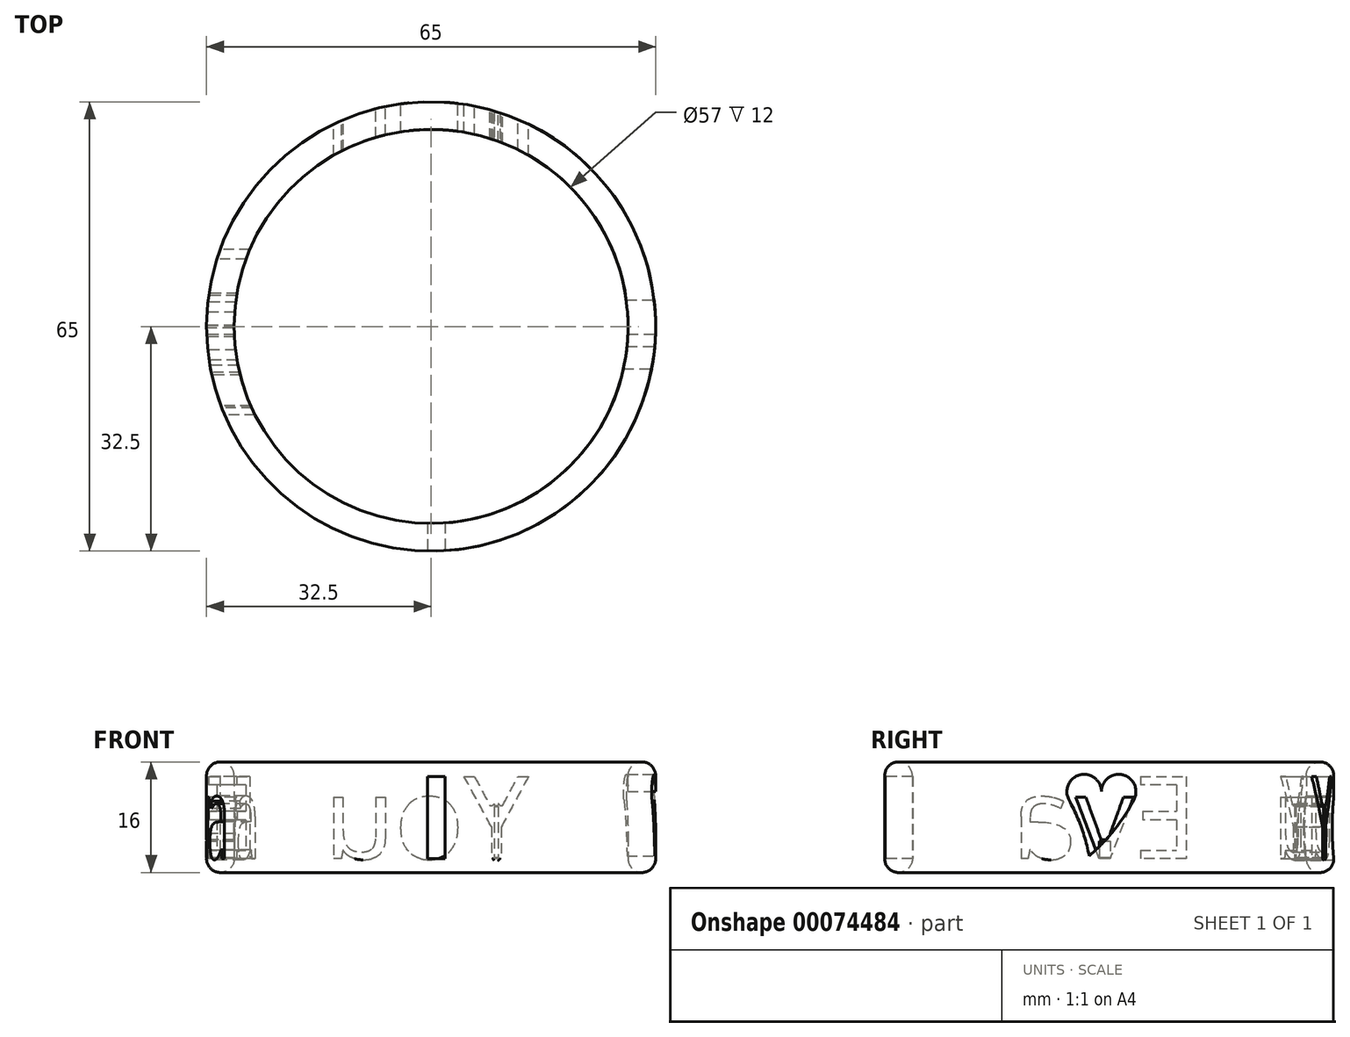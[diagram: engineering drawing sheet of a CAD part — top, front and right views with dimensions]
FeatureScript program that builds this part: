
annotation { "Feature Type Name" : "Feature", "Feature Type Description" : "" }
export const myFeature = defineFeature(function(context is Context, id is Id, definition is map)
    precondition{}
    {
        {
            var Q0;
            Q0=qCreatedBy(makeId("Top.planeOp"),FACE);
            var sketch = newSketch(context, id + "F0", { "sketchPlane" : qUnion([Q0])});
            skCircle(sketch, "E0", {"center": v(0, 0) * mm, "radius": 28.5 * mm});
            skCircle(sketch, "E1", {"center": v(0, 0) * mm, "radius": 32.5 * mm});
            skSolve(sketch);
        }
        {
            var Q0;
            Q0=makeQuery(id+"F0.imprint","IMPRINT",FACE,{"disambiguationData":[TD([[makeQuery(id+"F0.imprint","IMPRINT",EDGE,{"derivedFrom":sQuery(id+"F0.wireOp",EDGE,"E0")}),-1.0]])]});
            extrude(context, id + "F1", {"entities" : qUnion([Q0]), "depth" : 16 * mm});
        }
        {
            var Q0;
            Q0=qCreatedBy(makeId("Front.planeOp"),FACE);
            cPlane(context, id + "F2", {"entities" : qUnion([Q0]), "cplaneType" : CPlaneType.OFFSET, "offset" : 36 * mm, "width" : 150 * mm, "height" : 150 * mm});
        }
        {
            var Q0;
            Q0=qCreatedBy(id+"F2.planeOp",FACE);
            var sketch = newSketch(context, id + "F3", { "sketchPlane" : qUnion([Q0])});
            skText(sketch, "E2", { "text": "I", "fontName": "OpenSans-Bold.ttf"});
            skLineSegment(sketch, "E3.0", {"start": v(-28.5, 16) * mm, "end": v(28.5, 16) * mm});
            skLineSegment(sketch, "E4.0", {"start": v(-32.5, 0) * mm, "end": v(32.5, 0) * mm});
            const initialGuessF3  = {"E2": [-0.00201, 0.002, 1, 0, 0.012]};
            skSetInitialGuess(sketch, initialGuessF3);
            skSolve(sketch);
        }
        {
            var Q0;
            Q0 = qSketchRegion(id + "F3", true);
            extrude(context, id + "F4", {"entities" : qUnion([Q0]), "operationType" : NewBodyOperationType.REMOVE, "oppositeDirection" : true, "depth" : 25 * mm});
        }
        {
            var Q0;
            Q0=qCreatedBy(makeId("Right.planeOp"),FACE);
            cPlane(context, id + "F5", {"entities" : qUnion([Q0]), "cplaneType" : CPlaneType.OFFSET, "offset" : 35.5 * mm, "width" : 150 * mm, "height" : 150 * mm});
        }
        {
            var Q0;
            Q0=qCreatedBy(id+"F5.planeOp",FACE);
            var sketch = newSketch(context, id + "F6", { "sketchPlane" : qUnion([Q0])});
            skLineSegment(sketch, "E5.0", {"start": v(-32.5, 16) * mm, "end": v(32.5, 16) * mm});
            skLineSegment(sketch, "E6", {"start": v(-32.5, 0) * mm, "end": v(-32.5, 16) * mm});
            skLineSegment(sketch, "E7", {"start": v(32.5, 16) * mm, "end": v(32.5, 0) * mm});
            skLineSegment(sketch, "E8.0", {"start": v(-32.5, 0) * mm, "end": v(32.5, 0) * mm});
            skCircle(sketch, "E9", {"center": v(-3.64, 11.7) * mm, "radius": 2.5 * mm});
            skCircle(sketch, "E10", {"center": v(1.36, 11.7) * mm, "radius": 2.5 * mm});
            skArc(sketch, "E11", {"start": v(-2.91, 2.4) * mm, "mid": v(-4.05, 6.56) * mm, "end": v(-5.83, 10.5) * mm});
            skArc(sketch, "E12", {"start": v(-2.91, 2.4) * mm, "mid": v(0.72, 6.16) * mm, "end": v(3.58, 10.54) * mm});
            skSolve(sketch);
        }
        {
            var Q0;
            {var subQ0=sQuery(id+"F6.wireOp",EDGE,"E11");Q0=makeQuery(id+"F6.imprint","IMPRINT",FACE,{"disambiguationData":[TD([[makeQuery(id+"F6.imprint","IMPRINT",EDGE,{"derivedFrom":subQ0}),-1.0]])]});}
            var Q1;
            {var subQ0=sQuery(id+"F6.wireOp",EDGE,"E9");var subQ1=makeQuery(id+"F6.imprint","INTERSECT",VERTEX,{"derivedFrom":[subQ0,sQuery(id+"F6.wireOp",EDGE,"E11")]});Q1=makeQuery(id+"F6.imprint","IMPRINT",FACE,{"disambiguationData":[TD([[makeQuery(id+"F6.imprint","IMPRINT",EDGE,{"disambiguationData":[TD([[subQ1,1.0]])],"derivedFrom":subQ0}),1.0]])]});}
            var Q2;
            {var subQ0=sQuery(id+"F6.wireOp",EDGE,"E10");var subQ1=makeQuery(id+"F6.imprint","INTERSECT",VERTEX,{"derivedFrom":[subQ0,sQuery(id+"F6.wireOp",EDGE,"E12")]});Q2=makeQuery(id+"F6.imprint","IMPRINT",FACE,{"disambiguationData":[TD([[makeQuery(id+"F6.imprint","IMPRINT",EDGE,{"disambiguationData":[TD([[subQ1,1.0]])],"derivedFrom":subQ0}),1.0]])]});}
            extrude(context, id + "F7", {"entities" : qUnion([Q0, Q1, Q2]), "operationType" : NewBodyOperationType.REMOVE, "oppositeDirection" : true, "depth" : 25 * mm});
        }
        {
            var Q0;
            Q0=qCreatedBy(makeId("Front.planeOp"),FACE);
            cPlane(context, id + "F8", {"entities" : qUnion([Q0]), "cplaneType" : CPlaneType.OFFSET, "offset" : 35.5 * mm, "oppositeDirection" : true, "width" : 150 * mm, "height" : 150 * mm});
        }
        {
            var Q0;
            Q0=qCreatedBy(id+"F8.planeOp",FACE);
            var sketch = newSketch(context, id + "F9", { "sketchPlane" : qUnion([Q0])});
            skLineSegment(sketch, "E13", {"start": v(-67.89, 7.43) * mm, "end": v(-67.89, 38.78) * mm});
            skSolve(sketch);
        }
        {
            var Q0;
            Q0=sQuery(id+"F9.wireOp",EDGE,"E13");
            cPlane(context, id + "F10", {"entities" : qUnion([Q0]), "cplaneType" : CPlaneType.LINE_ANGLE, "offset" : 150 * mm, "angle" : 90 * degree, "width" : 150 * mm, "height" : 150 * mm});
        }
        {
            var Q0;
            Q0=qCreatedBy(id+"F10.planeOp",FACE);
            var sketch = newSketch(context, id + "F11", { "sketchPlane" : qUnion([Q0])});
            skText(sketch, "E14", { "text": "You", "fontName": "OpenSans-Regular.ttf"});
            skLineSegment(sketch, "E15", {"start": v(-32.5, 0) * mm, "end": v(-32.5, 16) * mm});
            skLineSegment(sketch, "E16", {"start": v(32.5, 16) * mm, "end": v(32.5, 0) * mm});
            skLineSegment(sketch, "E17", {"start": v(-14.1, 9.7) * mm, "end": v(-4.18, 9.7) * mm});
            const initialGuessF11  = {"E14": [-0.0141, 0.002, 1, 0, 0.012]};
            skSetInitialGuess(sketch, initialGuessF11);
            skSolve(sketch);
        }
        {
            var Q0;
            Q0=qCreatedBy(makeId("Right.planeOp"),FACE);
            cPlane(context, id + "F12", {"entities" : qUnion([Q0]), "cplaneType" : CPlaneType.OFFSET, "offset" : 35.5 * mm, "oppositeDirection" : true, "width" : 150 * mm, "height" : 150 * mm});
        }
        {
            var Q0;
            Q0=qCreatedBy(id+"F12.planeOp",FACE);
            var sketch = newSketch(context, id + "F13", { "sketchPlane" : qUnion([Q0])});
            skLineSegment(sketch, "E18", {"start": v(-44.84, 4.54) * mm, "end": v(-44.84, -15.83) * mm});
            skSolve(sketch);
        }
        {
            var Q0;
            Q0=sQuery(id+"F13.wireOp",EDGE,"E18");
            cPlane(context, id + "F14", {"entities" : qUnion([Q0]), "cplaneType" : CPlaneType.LINE_ANGLE, "offset" : 150 * mm, "angle" : 0 * degree, "width" : 150 * mm, "height" : 150 * mm});
        }
        {
            var Q0;
            Q0=qCreatedBy(id+"F14.planeOp",FACE);
            var sketch = newSketch(context, id + "F15", { "sketchPlane" : qUnion([Q0])});
            skText(sketch, "E19", { "text": "Eva", "fontName": "OpenSans-Regular.ttf"});
            skLineSegment(sketch, "E20.0", {"start": v(-32.5, 16) * mm, "end": v(32.5, 16) * mm});
            skLineSegment(sketch, "E21.0", {"start": v(-32.5, 0) * mm, "end": v(32.5, 0) * mm});
            skLineSegment(sketch, "E22", {"start": v(-32.5, 0) * mm, "end": v(-32.5, 16) * mm});
            skLineSegment(sketch, "E23", {"start": v(32.5, 16) * mm, "end": v(32.5, 0) * mm});
            skLineSegment(sketch, "E24", {"start": v(0, 0) * mm, "end": v(0, 16) * mm, "construction": true});
            const initialGuessF15  = {"E19": [-0.01277, 0.002, 1, 0, 0.012]};
            skSetInitialGuess(sketch, initialGuessF15);
            skSolve(sketch);
        }
        {
            var Q0;
            Q0=makeQuery(id+"F15.imprint","IMPRINT",FACE,{"disambiguationData":[TD([[makeQuery(id+"F15.imprint","IMPRINT",EDGE,{"derivedFrom":sQuery(id+"F15.wireOp",EDGE,"E19.sketch_text.stroke-0")}),-1.0]])]});
            var Q1;
            Q1=makeQuery(id+"F15.imprint","IMPRINT",FACE,{"disambiguationData":[TD([[makeQuery(id+"F15.imprint","IMPRINT",EDGE,{"derivedFrom":sQuery(id+"F15.wireOp",EDGE,"E19.sketch_text.stroke-12")}),-1.0]])]});
            var Q2;
            Q2=makeQuery(id+"F15.imprint","IMPRINT",FACE,{"disambiguationData":[TD([[makeQuery(id+"F15.imprint","IMPRINT",EDGE,{"derivedFrom":sQuery(id+"F15.wireOp",EDGE,"E19.sketch_text.stroke-22")}),-1.0]])]});
            var Q3;
            Q3=makeQuery(id+"F15.imprint","IMPRINT",FACE,{"disambiguationData":[TD([[makeQuery(id+"F15.imprint","IMPRINT",EDGE,{"derivedFrom":sQuery(id+"F15.wireOp",EDGE,"E19.sketch_text.stroke-41")}),1.0]])]});
            extrude(context, id + "F16", {"entities" : qUnion([Q0, Q1, Q2, Q3]), "operationType" : NewBodyOperationType.REMOVE, "oppositeDirection" : true, "depth" : 25 * mm});
        }
        {
            var Q0;
            Q0 = qSketchRegion(id + "F11", true);
            var Q1;
            Q1=makeQuery(id+"F11.imprint","IMPRINT",FACE,{"disambiguationData":[TD([[makeQuery(id+"F11.imprint","IMPRINT",EDGE,{"derivedFrom":sQuery(id+"F11.wireOp",EDGE,"E14.sketch_text.stroke-18")}),1.0]])]});
            extrude(context, id + "F17", {"entities" : qUnion([Q0, Q1]), "operationType" : NewBodyOperationType.REMOVE, "oppositeDirection" : true, "depth" : 25 * mm});
        }
        {
            var Q0;
            Q0=makeQuery(id+"F1.opExtrude","CAP_FACE",FACE,{"disambiguationData":[OSD([sQuery(id+"F0.wireOp",EDGE,"E0"),sQuery(id+"F0.wireOp",EDGE,"E1")])],"isStart":false});
            var Q1;
            Q1=makeQuery(id+"F1.opExtrude","CAP_FACE",FACE,{"disambiguationData":[OSD([sQuery(id+"F0.wireOp",EDGE,"E0"),sQuery(id+"F0.wireOp",EDGE,"E1")])],"isStart":true});
            fillet(context, id + "F18", {"entities" : qUnion([Q0, Q1]), "radius" : 2 * mm, "tangentPropagation" : true, "allowEdgeOverflow" : false});
        }
        {
            var Q0;
            Q0=makeQuery(id+"F16.boolean.opBoolean","COPY",FACE,{"derivedFrom":makeQuery(id+"F16.opExtrude","SWEPT_FACE",FACE,{"disambiguationData":[OSD([sQuery(id+"F15.wireOp",EDGE,"E19.sketch_text.stroke-16")])]})});
            extrude(context, id + "F19", {"entities" : qUnion([Q0]), "operationType" : NewBodyOperationType.REMOVE, "oppositeDirection" : true, "depth" : 1.5 * mm, "hasDraft" : true, "draftAngle" : 45 * degree});
        }
        {
            var Q0;
            Q0=makeQuery(id+"F16.boolean.opBoolean","COPY",FACE,{"derivedFrom":makeQuery(id+"F16.opExtrude","SWEPT_FACE",FACE,{"disambiguationData":[OSD([sQuery(id+"F15.wireOp",EDGE,"E19.sketch_text.stroke-21")])]})});
            var sketch = newSketch(context, id + "F20", { "sketchPlane" : qUnion([Q0])});
            skSolve(sketch);
        }
        {
            var Q0;
            {var subQ0=sQuery(id+"F15.wireOp",EDGE,"E19.sketch_text.stroke-21");Q0=makeQuery(id+"F20.imprint","IMPRINT",FACE,{"disambiguationData":[TD([[makeQuery(id+"F20.imprint","IMPRINT",EDGE,{"derivedFrom":makeQuery(id+"F16.boolean.opBoolean","COPY",EDGE,{"derivedFrom":makeQuery(id+"F16.opExtrude","SWEPT_EDGE",EDGE,{"disambiguationData":[OSD([sQuery(id+"F15.wireOp",EDGE,"E19.sketch_text.stroke-12"),subQ0])]})})}),1.0]])]});}
            var Q1;
            Q1=makeQuery(id+"F19.boolean.opBoolean","COPY",FACE,{"derivedFrom":makeQuery(id+"F19.opExtrude","CAP_FACE",FACE,{"disambiguationData":[OSD([sQuery(id+"F15.wireOp",EDGE,"E19.sketch_text.stroke-16")])],"isStart":false})});
            extrude(context, id + "F21", {"entities" : qUnion([Q0]), "endBound" : BoundingType.UP_TO_SURFACE, "endBoundEntityFace" : qUnion([Q1]), "depth" : 2.5 * mm});
        }
        {
            var Q0;
            Q0=makeQuery(id+"F21.opExtrude","CAP_FACE",FACE,{"disambiguationData":[OSD([sQuery(id+"F0.wireOp",EDGE,"E0"),sQuery(id+"F0.wireOp",EDGE,"E1"),sQuery(id+"F15.wireOp",EDGE,"E19.sketch_text.stroke-12"),sQuery(id+"F15.wireOp",EDGE,"E19.sketch_text.stroke-20"),sQuery(id+"F15.wireOp",EDGE,"E19.sketch_text.stroke-21")])],"isStart":false});
            extrude(context, id + "F22", {"entities" : qUnion([Q0]), "operationType" : NewBodyOperationType.REMOVE, "oppositeDirection" : true, "depth" : .15 * mm});
        }
        {
            var Q0;
            Q0=makeQuery(id+"F21.opExtrude","CAP_FACE",FACE,{"disambiguationData":[OSD([sQuery(id+"F0.wireOp",EDGE,"E0"),sQuery(id+"F0.wireOp",EDGE,"E1"),sQuery(id+"F15.wireOp",EDGE,"E19.sketch_text.stroke-12"),sQuery(id+"F15.wireOp",EDGE,"E19.sketch_text.stroke-20"),sQuery(id+"F15.wireOp",EDGE,"E19.sketch_text.stroke-21")])],"isStart":true});
            extrude(context, id + "F23", {"entities" : qUnion([Q0]), "operationType" : NewBodyOperationType.REMOVE, "oppositeDirection" : true, "depth" : .15 * mm});
        }
        {
            var Q0;
            Q0=makeQuery(id+"F17.boolean.opBoolean","COPY",FACE,{"derivedFrom":makeQuery(id+"F17.opExtrude","SWEPT_FACE",FACE,{"disambiguationData":[OSD([sQuery(id+"F11.wireOp",EDGE,"E14.sketch_text.stroke-4")])]})});
            var Q1;
            Q1=makeQuery(id+"F17.boolean.opBoolean","COPY",FACE,{"derivedFrom":makeQuery(id+"F17.opExtrude","SWEPT_FACE",FACE,{"disambiguationData":[OSD([sQuery(id+"F11.wireOp",EDGE,"E17")])]})});
            extrude(context, id + "F24", {"entities" : qUnion([Q0]), "endBound" : BoundingType.UP_TO_SURFACE, "endBoundEntityFace" : qUnion([Q1]), "depth" : 25 * mm});
        }
        {
            var Q0;
            Q0=makeQuery(id+"F24.opExtrude","CAP_FACE",FACE,{"disambiguationData":[OSD([sQuery(id+"F11.wireOp",EDGE,"E14.sketch_text.stroke-4")])],"isStart":false});
            extrude(context, id + "F25", {"entities" : qUnion([Q0]), "operationType" : NewBodyOperationType.REMOVE, "oppositeDirection" : true, "depth" : .15 * mm});
        }
        {
            var Q0;
            Q0=makeQuery(id+"F24.opExtrude","CAP_FACE",FACE,{"disambiguationData":[OSD([sQuery(id+"F11.wireOp",EDGE,"E14.sketch_text.stroke-4")])],"isStart":true});
            extrude(context, id + "F26", {"entities" : qUnion([Q0]), "operationType" : NewBodyOperationType.REMOVE, "oppositeDirection" : true, "depth" : .15 * mm});
        }
        {
            var Q0;
            Q0=makeQuery(id+"F24.opExtrude","SWEPT_FACE",FACE,{"disambiguationData":[OSD([sQuery(id+"F11.wireOp",EDGE,"E14.sketch_text.stroke-3"),sQuery(id+"F11.wireOp",EDGE,"E14.sketch_text.stroke-4")])]});
            extrude(context, id + "F27", {"entities" : qUnion([Q0]), "operationType" : NewBodyOperationType.REMOVE, "oppositeDirection" : true, "depth" : .4 * mm, "hasDraft" : true, "draftAngle" : 45 * degree});
        }
        {
            var Q0;
            Q0=makeQuery(id+"F24.opExtrude","SWEPT_FACE",FACE,{"disambiguationData":[OSD([sQuery(id+"F11.wireOp",EDGE,"E14.sketch_text.stroke-4"),sQuery(id+"F11.wireOp",EDGE,"E14.sketch_text.stroke-5")])]});
            extrude(context, id + "F28", {"entities" : qUnion([Q0]), "operationType" : NewBodyOperationType.REMOVE, "oppositeDirection" : true, "depth" : .4 * mm, "hasDraft" : true, "draftAngle" : 45 * degree});
        }
    });
